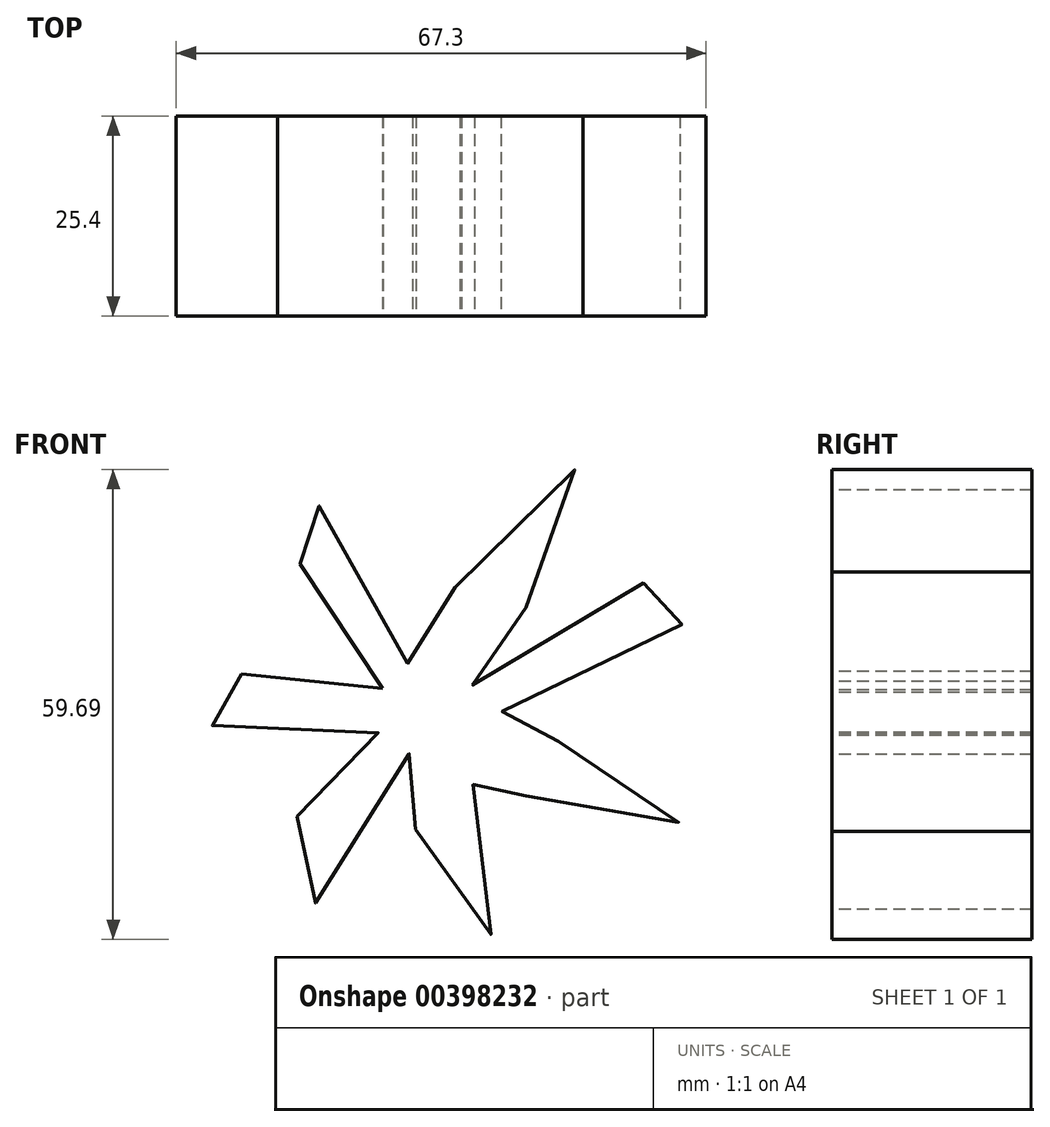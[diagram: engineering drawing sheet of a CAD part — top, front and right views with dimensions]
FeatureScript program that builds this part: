
annotation { "Feature Type Name" : "Feature", "Feature Type Description" : "" }
export const myFeature = defineFeature(function(context is Context, id is Id, definition is map)
    precondition{}
    {
        {
            var Q0;
            Q0=qCreatedBy(makeId("Front.planeOp"),FACE);
            var sketch = newSketch(context, id + "F0", { "sketchPlane" : qUnion([Q0])});
            skFitSpline(sketch, "E0", {"points": [v(-7.25, 5.85) * mm, v(-14.97, 17.08) * mm, v(-20.12, 30.88) * mm, v(-8.19, 20.82) * mm, v(-3.04, 6.78) * mm, v(4.21, 22.93) * mm, v(17.55, 33.45) * mm, v(12.4, 18.25) * mm, v(2.57, 5.38) * mm, v(18.72, 15.9) * mm, v(33.69, 19.89) * mm, v(21.76, 7.25) * mm, v(4.45, 1.87) * mm, v(20.35, -2.57) * mm, v(30.41, -11) * mm, v(14.97, -9.83) * mm, v(2.8, -2.57) * mm, v(7.02, -13.57) * mm, v(5.61, -25.97) * mm, v(-2.8, -13.57) * mm, v(-3.04, 0) * mm, v(-9.6, -15.2) * mm, v(-19.65, -21.76) * mm, v(-16.14, -7.49) * mm, v(-7.25, 0) * mm, v(-21.76, 0) * mm, v(-33.45, 4.21) * mm, v(-18.01, 7.95) * mm, v(-7.25, 5.85) * mm]});
            skSolve(sketch);
        }
        {
            var Q0;
            Q0=sQuery(id+"F0.wireOp",EDGE,"E0");
            extrude(context, id + "F1", {"bodyType" : ToolBodyType.SURFACE, "surfaceEntities" : qUnion([Q0]), "depth" : 25.4 * mm});
        }
    });
